# Revit family: PRD_FrankeWS_UrnlFlshngVlvs_F5EUrinalFlushValveForConcealedMounting_F5EF3002
name_source: partatom
category: Plumbing Fixtures
revit_build: Autodesk Revit 2018 (Build: 20190510_1515(x64)
units: mm (PartAtom-declared; Revit-internal decimal feet)

## family parameters
Cut with Voids When Loaded = Yes
Host = Face
OmniClass Number = 23.45.05.14.99
OmniClass Title = Other Sanitary Washing Plumbing Fixtures
Part Type = Normal
Room Calculation Point = No
Round Connector Dimension = Use Diameter
Shared = No

## types (1)
- F5EF3002
    ApparentLoad = 0 VA
    AssetType = Fixed
    BIMObjectName = PRD_AR_UrinalFlushingValves_F5EUrinalFlushValveForConcealedMounting_F5EF3002
    Category = Pr_40_20_93_79, Urinal flushing valves
    Default Elevation = 850 mm  [stored 2.78871 ft]
    DefaultAutomaticHygieneFlushing = 24h after the last activity
    Description = F5E Urinal flush valve DN 15 for concealed mounting, opto-electronic control. With round sensor (diameter 55 mm), with integrated control electronics and deactivation of cleaning, high-polished chrome-plated brass, to be screwed in from rear, with anti-twist protection, solenoid valve with screw fixings G 1/2 B, extension cable for solenoid valve and connection cable for power supply, each 5 m long. Activated water hygiene flushing 24 hours after last activation and saving of statistical data. With option for parameterization and communication via optional, bidirectional remote control. Optional for battery operation with 6 V lithium battery (CR-P2) per fitting or separate power supply via power supply unit 6.75 V/12 V DC or AQUA 3000 open system accessories. Battery compartment including battery or power supply unit with extension cable must be ordered separately.
    DiameterNominal = 15.000 mm
    DurationUnit = year
    Features = Opto-electronic control. High-polished chrome-plated brass
    Finish = Polished chrome
    FunctionalPrinciple = Electronic self-closing
    GrossWeight = 0.69 kg
    IfcExportAs = IfcSanitaryTerminalType
    IfcExportType = USERDEFINED
    InletSize = DN 15
    IntegralAccessories = Battery compartment including battery or power supply unit with extension cable must be ordered separately.
    Manufacturer = KWC Group AG
    ManufacturerName = KWC Group AG
    ManufacturerURL = www.kwc.com
    Material = Brass
    MaterialFitting = Synthetic
    MaximumFlowPressure = 4.00 bar
    MaximumFlushWaterVolume = 4.00 liter
    MaximumFlushingFlow = 0.70 liter per second
    MinimumFlowPressure = 1.00 bar
    MinimumFlushWaterVolume = 2.00 liter
    MinimumFlushingFlow = 0.30 liter per second
    Model = F5EF3002
    ModelNumber = 2030062317
    ModelReference = F5EF3002
    NBSDescription = Urinal flushing valves
    NBSReference = 45-35-70/355
    Name = F5E Urinal flush valve for concealed mounting F5EF3002
    NetWeight = 0.00 kg
    NominalDepth = 0 mm  [stored 0 ft]
    NominalHeight = 0 mm  [stored 0 ft]
    NominalLength = 0 mm  [stored 0 ft]
    NominalWidth = 0 mm  [stored 0 ft]
    PowerFactor = 1
    PowerSupplyConnection = 6,75 / 12 V DC / A3000 open
    ProductCode = 209.0630.475
    ProductInformation = https://pim.kwc.com
    ProtectiveShutdown = Yes
    SoundInsulation = No
    Status = New
    TailorMade = No
    TypeOfFlushingFitting = Urinal flush valve
    TypeOfMounting = Concealed mounting
    TypeOfOperation = Sensor operation
    TypeOfSensor = Opto-electronic sensor
    URL = www.kwc.com
    Uniclass2015Code = Pr_40_20_93_79
    Uniclass2015Title = Urinal flushing valves
    Uniclass2015Version = Products v1.17
    ValveMaterial = PRD_AR_ChromatedBrass_HighPolished
    Version = 1
    Voltage = 12 V
    WarrantyDurationUnit = year

note: [stored X ft] marks values corroborated as IEEE doubles in the binary element streams (Revit-internal decimal feet)

## geometry (parser evidence)
native form markers: Sweep x5
no freeform markers — native parametric forms only
